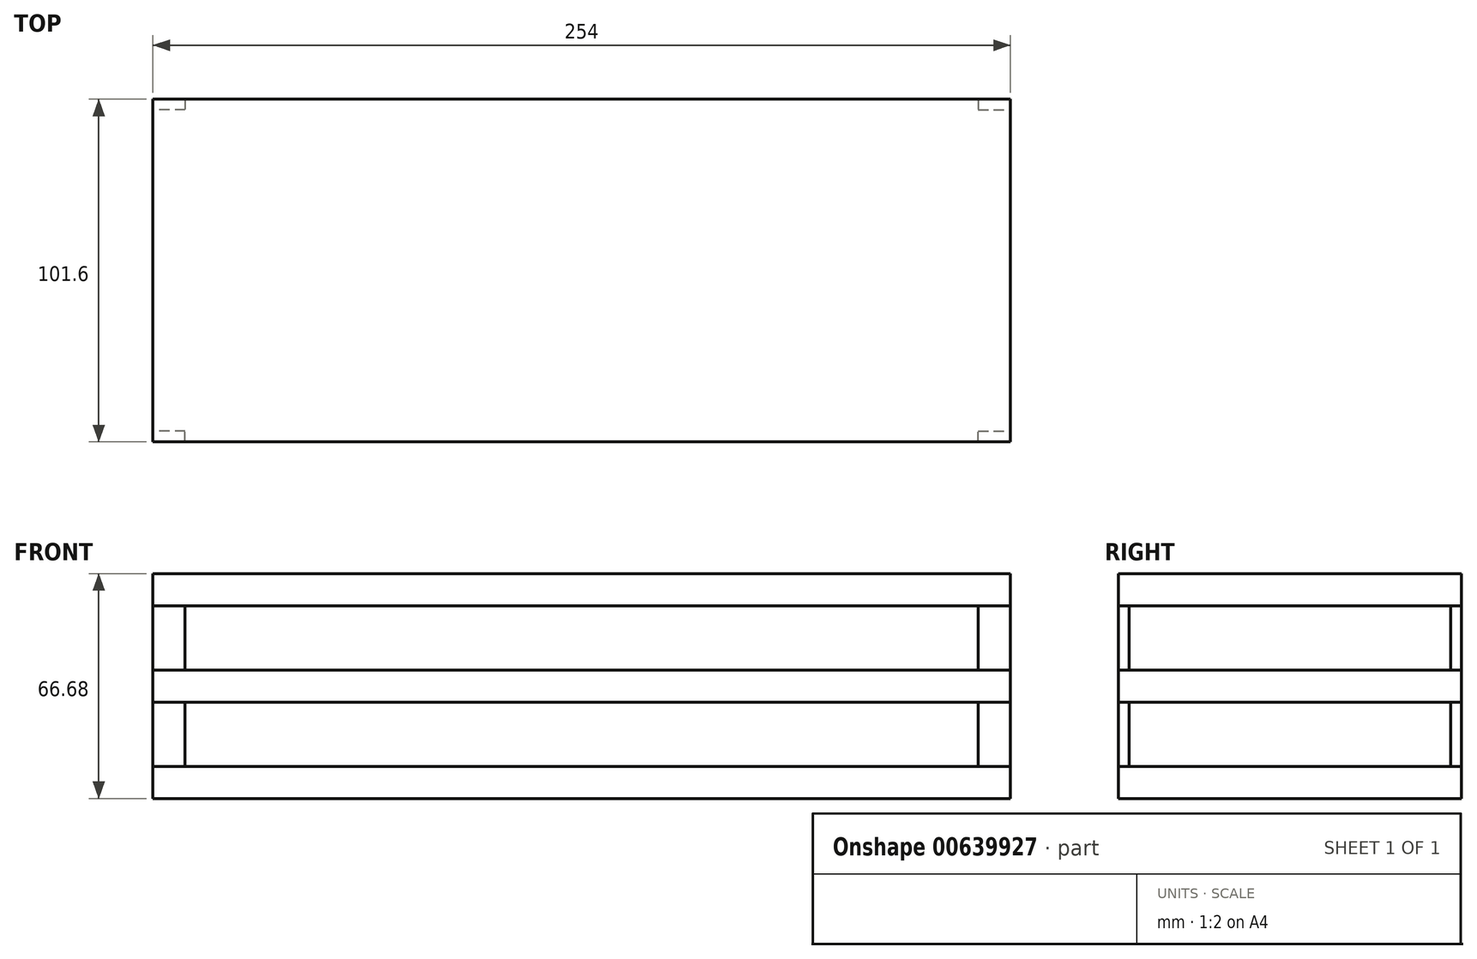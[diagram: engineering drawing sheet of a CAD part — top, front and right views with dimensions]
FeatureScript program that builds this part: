
annotation { "Feature Type Name" : "Feature", "Feature Type Description" : "" }
export const myFeature = defineFeature(function(context is Context, id is Id, definition is map)
    precondition{}
    {
        {
            var Q0;
            Q0=qCreatedBy(makeId("Front.planeOp"),FACE);
            var sketch = newSketch(context, id + "F0", { "sketchPlane" : qUnion([Q0])});
            skLineSegment(sketch, "E0", {"start": v(-30.22, -4.64) * mm, "end": v(-30.22, -14.17) * mm});
            skLineSegment(sketch, "E1", {"start": v(-30.22, -4.64) * mm, "end": v(223.78, -4.64) * mm});
            skLineSegment(sketch, "E2", {"start": v(223.78, -4.64) * mm, "end": v(223.78, -14.17) * mm});
            skLineSegment(sketch, "E3", {"start": v(223.78, -14.17) * mm, "end": v(-30.22, -14.17) * mm});
            skSolve(sketch);
        }
        {
            var Q0;
            Q0=makeQuery(id+"F0.imprint","IMPRINT",FACE,{"disambiguationData":[TD([[makeQuery(id+"F0.imprint","IMPRINT",EDGE,{"derivedFrom":sQuery(id+"F0.wireOp",EDGE,"E0")}),1.0]])]});
            extrude(context, id + "F1", {"entities" : qUnion([Q0]), "depth" : 101.6 * mm, "offsetDistance" : 25.4 * mm});
        }
        {
            var Q0;
            Q0=makeQuery(id+"F1.opExtrude","SWEPT_FACE",FACE,{"disambiguationData":[OSD([sQuery(id+"F0.wireOp",EDGE,"E1")])]});
            var sketch = newSketch(context, id + "F2", { "sketchPlane" : qUnion([Q0])});
            skLineSegment(sketch, "E4", {"start": v(223.78, -101.6) * mm, "end": v(214.25, -101.6) * mm});
            skLineSegment(sketch, "E5", {"start": v(214.25, -101.6) * mm, "end": v(214.25, -98.43) * mm});
            skLineSegment(sketch, "E6", {"start": v(214.25, -98.43) * mm, "end": v(223.78, -98.43) * mm});
            skLineSegment(sketch, "E7", {"start": v(223.78, -98.43) * mm, "end": v(223.78, -101.6) * mm});
            skLineSegment(sketch, "E8", {"start": v(223.78, 0) * mm, "end": v(214.25, 0) * mm});
            skLineSegment(sketch, "E9", {"start": v(214.25, 0) * mm, "end": v(214.25, -3.18) * mm});
            skLineSegment(sketch, "E10", {"start": v(214.25, -3.18) * mm, "end": v(223.78, -3.18) * mm});
            skLineSegment(sketch, "E11", {"start": v(223.78, -3.18) * mm, "end": v(223.78, 0) * mm});
            skLineSegment(sketch, "E12", {"start": v(-30.22, 0) * mm, "end": v(-20.7, 0) * mm});
            skLineSegment(sketch, "E13", {"start": v(-20.7, 0) * mm, "end": v(-20.7, -3.17) * mm});
            skLineSegment(sketch, "E14", {"start": v(-20.7, -3.17) * mm, "end": v(-30.22, -3.18) * mm});
            skLineSegment(sketch, "E15", {"start": v(-30.22, -3.18) * mm, "end": v(-30.22, 0) * mm});
            skLineSegment(sketch, "E16", {"start": v(-30.22, -101.6) * mm, "end": v(-20.7, -101.6) * mm});
            skLineSegment(sketch, "E17", {"start": v(-20.7, -101.6) * mm, "end": v(-20.7, -98.43) * mm});
            skLineSegment(sketch, "E18", {"start": v(-20.7, -98.43) * mm, "end": v(-30.22, -98.43) * mm});
            skLineSegment(sketch, "E19", {"start": v(-30.22, -98.43) * mm, "end": v(-30.22, -101.6) * mm});
            skSolve(sketch);
        }
        {
            var Q0;
            Q0=makeQuery(id+"F2.imprint","IMPRINT",FACE,{"disambiguationData":[TD([[makeQuery(id+"F2.imprint","IMPRINT",EDGE,{"derivedFrom":sQuery(id+"F2.wireOp",EDGE,"E4")}),1.0]])]});
            var Q1;
            Q1=makeQuery(id+"F2.imprint","IMPRINT",FACE,{"disambiguationData":[TD([[makeQuery(id+"F2.imprint","IMPRINT",EDGE,{"derivedFrom":sQuery(id+"F2.wireOp",EDGE,"E8")}),-1.0]])]});
            var Q2;
            Q2=makeQuery(id+"F2.imprint","IMPRINT",FACE,{"disambiguationData":[TD([[makeQuery(id+"F2.imprint","IMPRINT",EDGE,{"derivedFrom":sQuery(id+"F2.wireOp",EDGE,"E16")}),1.0]])]});
            var Q3;
            Q3=makeQuery(id+"F2.imprint","IMPRINT",FACE,{"disambiguationData":[TD([[makeQuery(id+"F2.imprint","IMPRINT",EDGE,{"derivedFrom":sQuery(id+"F2.wireOp",EDGE,"E12")}),-1.0]])]});
            extrude(context, id + "F3", {"entities" : qUnion([Q0, Q1, Q2, Q3]), "depth" : 19.05 * mm, "offsetDistance" : 25.4 * mm});
        }
        {
            var Q0;
            Q0=makeQuery(id+"F3.opExtrude","CAP_FACE",FACE,{"disambiguationData":[OSD([sQuery(id+"F2.wireOp",EDGE,"E12"),sQuery(id+"F2.wireOp",EDGE,"E13"),sQuery(id+"F2.wireOp",EDGE,"E14"),sQuery(id+"F2.wireOp",EDGE,"E15")])],"isStart":false});
            var sketch = newSketch(context, id + "F4", { "sketchPlane" : qUnion([Q0])});
            skLineSegment(sketch, "E20", {"start": v(-30.22, 0) * mm, "end": v(-30.22, -101.6) * mm});
            skLineSegment(sketch, "E21", {"start": v(-30.22, -101.6) * mm, "end": v(223.78, -101.6) * mm});
            skLineSegment(sketch, "E22", {"start": v(223.78, -101.6) * mm, "end": v(223.78, 0) * mm});
            skLineSegment(sketch, "E23", {"start": v(223.78, 0) * mm, "end": v(-30.22, 0) * mm});
            skSolve(sketch);
        }
        {
            var Q0;
            Q0 = qSketchRegion(id + "F4", true);
            extrude(context, id + "F5", {"entities" : qUnion([Q0]), "depth" : 9.52 * mm, "offsetDistance" : 25.4 * mm});
        }
        {
            var Q0;
            Q0=makeQuery(id+"F5.opExtrude","CAP_FACE",FACE,{"disambiguationData":[OSD([sQuery(id+"F4.wireOp",EDGE,"E20"),sQuery(id+"F4.wireOp",EDGE,"E21"),sQuery(id+"F4.wireOp",EDGE,"E22"),sQuery(id+"F4.wireOp",EDGE,"E23")])],"isStart":false});
            var sketch = newSketch(context, id + "F6", { "sketchPlane" : qUnion([Q0])});
            skLineSegment(sketch, "E24", {"start": v(-30.22, 0) * mm, "end": v(-20.7, 0) * mm});
            skLineSegment(sketch, "E25", {"start": v(-20.7, 0) * mm, "end": v(-20.7, -3.18) * mm});
            skLineSegment(sketch, "E26", {"start": v(-20.7, -3.18) * mm, "end": v(-30.22, -3.18) * mm});
            skLineSegment(sketch, "E27", {"start": v(-30.22, -3.18) * mm, "end": v(-30.22, 0) * mm});
            skLineSegment(sketch, "E28", {"start": v(223.78, 0) * mm, "end": v(214.25, 0) * mm});
            skLineSegment(sketch, "E29", {"start": v(214.25, 0) * mm, "end": v(214.25, -3.17) * mm});
            skLineSegment(sketch, "E30", {"start": v(214.25, -3.17) * mm, "end": v(223.78, -3.17) * mm});
            skLineSegment(sketch, "E31", {"start": v(223.78, -3.17) * mm, "end": v(223.78, 0) * mm});
            skLineSegment(sketch, "E32", {"start": v(223.78, -101.6) * mm, "end": v(214.25, -101.6) * mm});
            skLineSegment(sketch, "E33", {"start": v(214.25, -101.6) * mm, "end": v(214.25, -98.43) * mm});
            skLineSegment(sketch, "E34", {"start": v(214.25, -98.43) * mm, "end": v(223.78, -98.43) * mm});
            skLineSegment(sketch, "E35", {"start": v(223.78, -98.43) * mm, "end": v(223.78, -101.6) * mm});
            skLineSegment(sketch, "E36", {"start": v(-30.22, -101.6) * mm, "end": v(-20.7, -101.6) * mm});
            skLineSegment(sketch, "E37", {"start": v(-20.7, -101.6) * mm, "end": v(-20.7, -98.43) * mm});
            skLineSegment(sketch, "E38", {"start": v(-20.7, -98.43) * mm, "end": v(-30.22, -98.43) * mm});
            skLineSegment(sketch, "E39", {"start": v(-30.22, -98.43) * mm, "end": v(-30.22, -101.6) * mm});
            skSolve(sketch);
        }
        {
            var Q0;
            Q0 = qSketchRegion(id + "F6", true);
            extrude(context, id + "F7", {"entities" : qUnion([Q0]), "depth" : 19.05 * mm, "offsetDistance" : 25.4 * mm});
        }
        {
            var Q0;
            Q0=makeQuery(id+"F7.opExtrude","CAP_FACE",FACE,{"disambiguationData":[OSD([sQuery(id+"F6.wireOp",EDGE,"E24"),sQuery(id+"F6.wireOp",EDGE,"E25"),sQuery(id+"F6.wireOp",EDGE,"E26"),sQuery(id+"F6.wireOp",EDGE,"E27")])],"isStart":false});
            var sketch = newSketch(context, id + "F8", { "sketchPlane" : qUnion([Q0])});
            skLineSegment(sketch, "E40", {"start": v(-30.22, 0) * mm, "end": v(-30.22, -101.6) * mm});
            skLineSegment(sketch, "E41", {"start": v(-30.22, -101.6) * mm, "end": v(223.78, -101.6) * mm});
            skLineSegment(sketch, "E42", {"start": v(223.78, -101.6) * mm, "end": v(223.78, 0) * mm});
            skLineSegment(sketch, "E43", {"start": v(223.78, 0) * mm, "end": v(-30.22, 0) * mm});
            skSolve(sketch);
        }
        {
            var Q0;
            Q0 = qSketchRegion(id + "F8", true);
            extrude(context, id + "F9", {"entities" : qUnion([Q0]), "depth" : 9.52 * mm, "offsetDistance" : 25.4 * mm});
        }
    });
